# Revit family: PRD_AR_TpsAndWtrSpplOtltFttngs_BatteryCompartment_ACEX9023
name_source: partatom
category: Specialty Equipment
units: mm (PartAtom-declared; Revit-internal decimal feet)

## family parameters
Always vertical = Yes
Cut with Voids When Loaded = No
Enable Cutting in Views = No
Maintain Annotation Orientation = No
OmniClass Number = 23.80.10.24.11
OmniClass Title = Batteries
Part Type = Normal
Room Calculation Point = No
Round Connector Dimension = Use Diameter
Shared = No
Work Plane-Based = No

## types (1)
- ACEX9023
    AssetType = Fixed
    BIMObjectName = PRD_AR_TapsAndWaterSupplyOutletFittings_BatteryCompartment_ACEX9023
    BodyMaterial = PRD_AR_Plastic_White
    Category = Pr_40_20_87, Taps and water supply outlet fittings
    Communication = no
    CompatibleA3000 = no
    CompatibleA3000Open = no
    Default Elevation = 0 mm  [stored 0 ft]
    Description = Battery compartment with holder and 6 V lithium battery (CR-P2).
    Export Type to IFC As = IfcSanitaryTerminalType
    Features = Battery compartment including 6 V battery
    IfcExportAs = IfcSanitaryTerminalType
    IfcExportType = USERDEFINED
    Manufacturer = KWC Group Management AG
    ManufacturerName = KWC Group Management AG
    ManufacturerURL = www.kwc-professional.com
    Model = ACEX9023
    ModelNumber = 3600002063
    ModelReference = ACEX9023
    Name = Battery compartment ACEX9023
    NominalDepth = 30 mm  [stored 0.0984252 ft]
    NominalHeight = 63 mm  [stored 0.206693 ft]
    NominalLength = 63 mm  [stored 0.206693 ft]
    NominalWidth = 37 mm  [stored 0.121391 ft]
    NumberOfBatteries = 1
    OutputVoltage = 6 Volt
    OutputVoltageUOM = DC
    PowerSwitch = no
    ProductInformation = http://pim.kwc.com
    ProtectiveSystemIP = IP57
    Status = New
    Type IFC Predefined Type = USERDEFINED
    TypeOfBatteries = CR-P2 Lithium battery 6V
    URL = www.kwc-professional.com
    Uniclass2015Code = Pr_40_20_87
    Uniclass2015Title = Taps and water supply outlet fittings
    Uniclass2015Version = Products v1.36
    Version = 1

note: [stored X ft] marks values corroborated as IEEE doubles in the binary element streams (Revit-internal decimal feet)

## geometry (parser evidence)
native form markers: Sweep x6
no freeform markers — native parametric forms only
